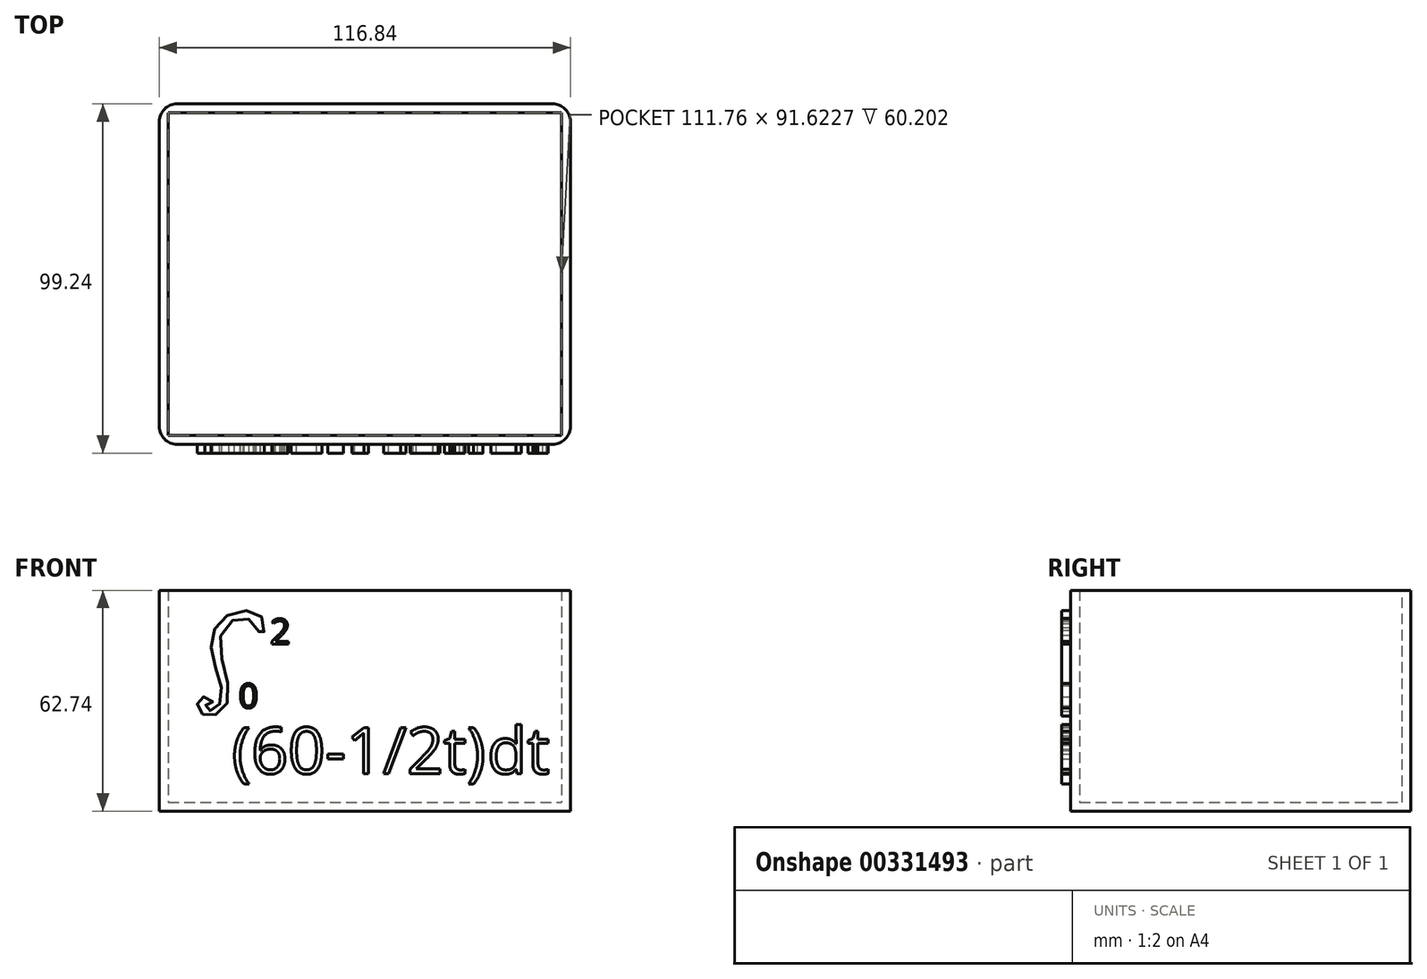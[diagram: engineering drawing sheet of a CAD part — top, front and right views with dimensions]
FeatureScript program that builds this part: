
annotation { "Feature Type Name" : "Feature", "Feature Type Description" : "" }
export const myFeature = defineFeature(function(context is Context, id is Id, definition is map)
    precondition{}
    {
        {
            var Q0;
            Q0=qCreatedBy(makeId("Right.planeOp"),FACE);
            var sketch = newSketch(context, id + "F0", { "sketchPlane" : qUnion([Q0])});
            skLineSegment(sketch, "E0", {"start": v(-49.21, 0) * mm, "end": v(-49.21, -62.74) * mm});
            skLineSegment(sketch, "E1", {"start": v(-49.21, -62.74) * mm, "end": v(47.49, -62.74) * mm});
            skLineSegment(sketch, "E2", {"start": v(47.49, -62.74) * mm, "end": v(47.49, 0) * mm});
            skLineSegment(sketch, "E3", {"start": v(47.49, 0) * mm, "end": v(0, 0) * mm});
            skLineSegment(sketch, "E4", {"start": v(0, 0) * mm, "end": v(-49.21, 0) * mm});
            skSolve(sketch);
        }
        {
            var Q0;
            Q0=makeQuery(id+"F0.imprint","IMPRINT",FACE,{"disambiguationData":[TD([[makeQuery(id+"F0.imprint","IMPRINT",EDGE,{"derivedFrom":sQuery(id+"F0.wireOp",EDGE,"E0")}),1.0]])]});
            extrude(context, id + "F1", {"entities" : qUnion([Q0]), "oppositeDirection" : true, "depth" : 57.15 * mm});
        }
        {
            var Q0;
            Q0=makeQuery(id+"F1.opExtrude","CAP_FACE",FACE,{"disambiguationData":[OSD([sQuery(id+"F0.wireOp",EDGE,"E0"),sQuery(id+"F0.wireOp",EDGE,"E1"),sQuery(id+"F0.wireOp",EDGE,"E2"),sQuery(id+"F0.wireOp",EDGE,"E3"),sQuery(id+"F0.wireOp",EDGE,"E4")])],"isStart":true});
            extrude(context, id + "F2", {"entities" : qUnion([Q0]), "operationType" : NewBodyOperationType.ADD, "depth" : 59.69 * mm});
        }
        {
            var Q0;
            Q0=qCreatedBy(makeId("Top.planeOp"),FACE);
            var sketch = newSketch(context, id + "F3", { "sketchPlane" : qUnion([Q0])});
            skLineSegment(sketch, "E5", {"start": v(-48.93, 41.44) * mm, "end": v(-48.93, -41.73) * mm});
            skLineSegment(sketch, "E6", {"start": v(-48.93, -41.73) * mm, "end": v(50.37, -41.73) * mm});
            skLineSegment(sketch, "E7", {"start": v(50.37, -41.73) * mm, "end": v(50.37, 41.44) * mm});
            skLineSegment(sketch, "E8", {"start": v(-48.93, 41.44) * mm, "end": v(50.37, 41.44) * mm});
            skSolve(sketch);
        }
        {
            var Q0;
            Q0=makeQuery(id+"F3.imprint","IMPRINT",FACE,{"disambiguationData":[TD([[makeQuery(id+"F3.imprint","IMPRINT",EDGE,{"derivedFrom":sQuery(id+"F3.wireOp",EDGE,"E5")}),1.0]])]});
            extrude(context, id + "F4", {"entities" : qUnion([Q0]), "operationType" : NewBodyOperationType.ADD, "oppositeDirection" : true, "depth" : 61.98 * mm});
        }
        {
            var Q0;
            {var subQ0=sQuery(id+"F0.wireOp",EDGE,"E4");var subQ1=sQuery(id+"F0.wireOp",EDGE,"E3");Q0=makeQuery(id+"F2.boolean.opBoolean","MERGE",FACE,{"derivedFrom":[makeQuery(id+"F1.opExtrude","SWEPT_FACE",FACE,{"disambiguationData":[OSD([subQ1,subQ0])]}),makeQuery(id+"F2.opExtrude","SWEPT_FACE",FACE,{"disambiguationData":[OSD([subQ1,subQ0])]})]});}
            shell(context, id + "F5", {"entities" : qUnion([Q0]), "thickness" : 2.54 * mm});
        }
        {
            var Q0;
            Q0=makeQuery(id+"F1.opExtrude","CAP_EDGE",EDGE,{"disambiguationData":[OSD([sQuery(id+"F0.wireOp",EDGE,"E0")])],"isStart":false});
            var Q1;
            Q1=makeQuery(id+"F2.opExtrude","CAP_EDGE",EDGE,{"disambiguationData":[OSD([sQuery(id+"F0.wireOp",EDGE,"E0")])],"isStart":false});
            var Q2;
            Q2=makeQuery(id+"F2.opExtrude","CAP_EDGE",EDGE,{"disambiguationData":[OSD([sQuery(id+"F0.wireOp",EDGE,"E2")])],"isStart":false});
            var Q3;
            Q3=makeQuery(id+"F1.opExtrude","CAP_EDGE",EDGE,{"disambiguationData":[OSD([sQuery(id+"F0.wireOp",EDGE,"E2")])],"isStart":false});
            fillet(context, id + "F6", {"entities" : qUnion([Q0, Q1, Q2, Q3]), "radius" : 5.08 * mm, "tangentPropagation" : true, "allowEdgeOverflow" : false});
        }
        {
            var Q0;
            {var subQ0=sQuery(id+"F0.wireOp",EDGE,"E0");Q0=makeQuery(id+"F2.boolean.opBoolean","MERGE",FACE,{"derivedFrom":[makeQuery(id+"F1.opExtrude","SWEPT_FACE",FACE,{"disambiguationData":[OSD([subQ0])]}),makeQuery(id+"F2.opExtrude","SWEPT_FACE",FACE,{"disambiguationData":[OSD([subQ0])]})]});}
            var sketch = newSketch(context, id + "F7", { "sketchPlane" : qUnion([Q0])});
            skFitSpline(sketch, "E9", {"points": [v(-39.72, -12.95) * mm, v(-37.38, -30.53) * mm, v(-43, -35.7) * mm, v(-46.36, -32.94) * mm, v(-44.66, -30.22) * mm, v(-41.95, -31.89) * mm, v(-44.13, -32.78) * mm, v(-42.5, -34.27) * mm, v(-39.33, -29.9) * mm, v(-42.36, -16.7) * mm, v(-37.77, -7.14) * mm, v(-28.04, -7.51) * mm, v(-27.92, -12.66) * mm, v(-31.95, -8.06) * mm, v(-39.72, -12.95) * mm]});
            skText(sketch, "E10", { "text": "2", "fontName": "OpenSans-Regular.ttf"});
            skText(sketch, "E11", { "text": "0", "fontName": "OpenSans-Regular.ttf"});
            skText(sketch, "E12", { "text": "(60-1/2t) ", "fontName": "OpenSans-Regular.ttf"});
            skText(sketch, "E13", { "text": "dt ", "fontName": "OpenSans-Regular.ttf"});
            const initialGuessF7  = {"E10": [-0.02561, -0.01525, 1, 0, 0.0072], "E11": [-0.03454, -0.03339, 1, 0, 0.0069], "E12": [-0.0365, -0.0521, 1, 0, 0.01324], "E13": [0.03604, -0.0521, 1, 0, 0.01324]};
            skSetInitialGuess(sketch, initialGuessF7);
            skSolve(sketch);
        }
        {
            var Q0;
            Q0 = qSketchRegion(id + "F7", true);
            extrude(context, id + "F8", {"entities" : qUnion([Q0]), "operationType" : NewBodyOperationType.ADD, "depth" : 2.54 * mm});
        }
    });
